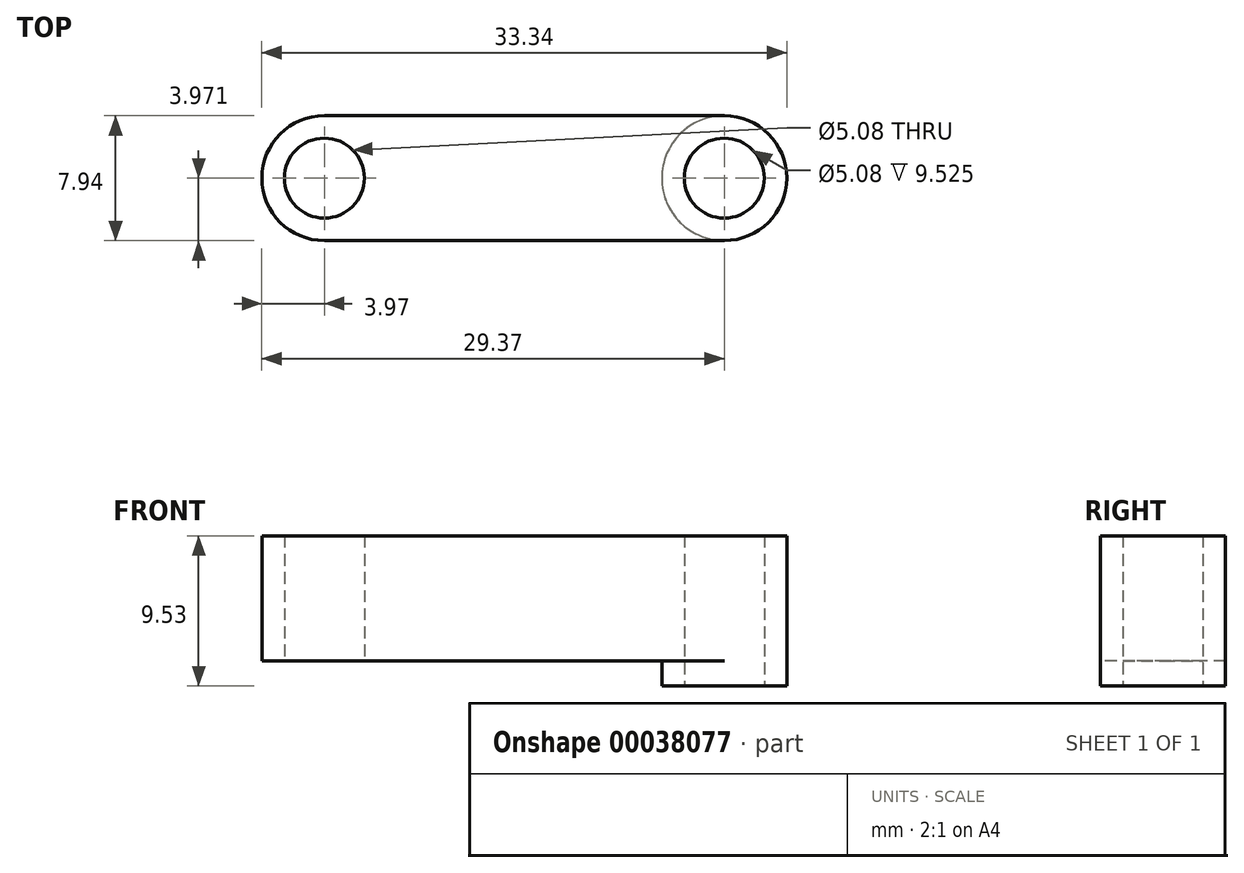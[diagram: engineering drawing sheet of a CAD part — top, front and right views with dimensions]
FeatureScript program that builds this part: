
annotation { "Feature Type Name" : "Feature", "Feature Type Description" : "" }
export const myFeature = defineFeature(function(context is Context, id is Id, definition is map)
    precondition{}
    {
        {
            var Q0;
            Q0=qCreatedBy(makeId("Top.planeOp"),FACE);
            var sketch = newSketch(context, id + "F0", { "sketchPlane" : qUnion([Q0])});
            skLineSegment(sketch, "E0.bottom", {"start": v(0, 0) * mm, "end": v(25.4, 0) * mm});
            skLineSegment(sketch, "E0.top", {"start": v(0, -7.94) * mm, "end": v(25.4, -7.94) * mm});
            skLineSegment(sketch, "E0.left", {"start": v(0, 0) * mm, "end": v(0, -7.94) * mm, "construction": true});
            skLineSegment(sketch, "E0.right", {"start": v(25.4, 0) * mm, "end": v(25.4, -7.94) * mm, "construction": true});
            skArc(sketch, "E1", {"start": v(0, 0) * mm, "mid": v(-3.97, -3.97) * mm, "end": v(0, -7.94) * mm});
            skArc(sketch, "E2", {"start": v(25.4, -7.94) * mm, "mid": v(29.37, -3.97) * mm, "end": v(25.4, 0) * mm});
            skCircle(sketch, "E3", {"center": v(0, -3.97) * mm, "radius": 2.54 * mm});
            skCircle(sketch, "E4", {"center": v(25.4, -3.97) * mm, "radius": 2.54 * mm});
            skSolve(sketch);
        }
        {
            var Q0;
            Q0 = qSketchRegion(id + "F0", true);
            extrude(context, id + "F1", {"entities" : qUnion([Q0]), "depth" : 7.94 * mm});
        }
        {
            var Q0;
            Q0=makeQuery(id+"F1.opExtrude","CAP_FACE",FACE,{"disambiguationData":[OSD([sQuery(id+"F0.wireOp",EDGE,"E0.bottom"),sQuery(id+"F0.wireOp",EDGE,"E0.top"),sQuery(id+"F0.wireOp",EDGE,"E1"),sQuery(id+"F0.wireOp",EDGE,"E2"),sQuery(id+"F0.wireOp",EDGE,"E3"),sQuery(id+"F0.wireOp",EDGE,"E4")])],"isStart":true});
            var sketch = newSketch(context, id + "F2", { "sketchPlane" : qUnion([Q0])});
            skCircle(sketch, "E5", {"center": v(25.4, 3.97) * mm, "radius": 3.97 * mm});
            skCircle(sketch, "E6", {"center": v(25.4, 3.97) * mm, "radius": 2.54 * mm});
            skSolve(sketch);
        }
        {
            var Q0;
            Q0 = qSketchRegion(id + "F2", true);
            extrude(context, id + "F3", {"entities" : qUnion([Q0]), "operationType" : NewBodyOperationType.ADD, "depth" : 1.59 * mm});
        }
    });
